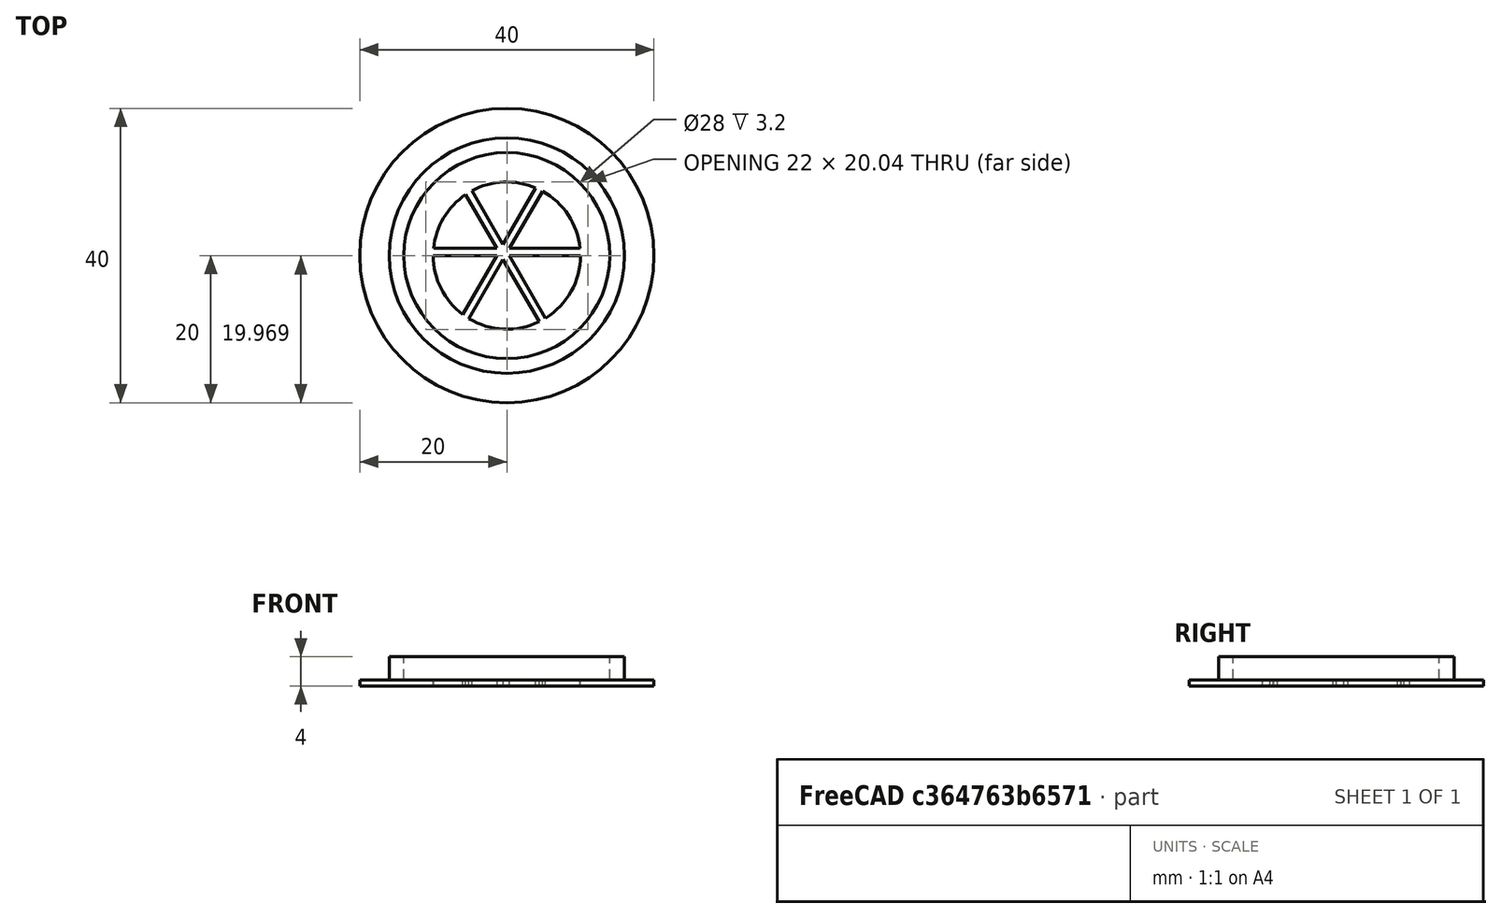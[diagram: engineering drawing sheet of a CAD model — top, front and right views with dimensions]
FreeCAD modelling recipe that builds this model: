
FCSTD DOCUMENT  (FreeCAD 0.17R13541 (Git))
Label: valve bottom 01
License: All rights reserved
LicenseURL: http://en.wikipedia.org/wiki/All_rights_reserved
objects: Part::Cylinder×4, Part::Box×3, Part::Cut×2, Part::MultiFuse×1
note: 10 computed .brp shape members not serialized (recipe doc carries the construction recipe); baked Part::Feature solids carry a one-line shape summary decoded from their .brp

FEATURE [Part::Cylinder] Cylinder  label="plate_flat"
  Angle = 360
  AttacherType = Attacher::AttachEngine3D
  Height = 0.8
  Radius = 20
FEATURE [Part::Cylinder] Cylinder001  label="hole"
  Angle = 360
  AttacherType = Attacher::AttachEngine3D
  Height = 1
  Radius = 10
FEATURE [Part::Cut] Cut  label="plate"
  Base = -> Cylinder
  Tool = -> Cylinder001
FEATURE [Part::Cylinder] Cylinder002  label="shoulder_out"
  Angle = 360
  AttacherType = Attacher::AttachEngine3D
  Height = 4
  Radius = 16
FEATURE [Part::Cylinder] Cylinder003  label="shoulder_in"
  Angle = 360
  AttacherType = Attacher::AttachEngine3D
  Height = 4
  Radius = 14
FEATURE [Part::Cut] Cut001  label="shoulder"
  Base = -> Cylinder002
  Tool = -> Cylinder003
FEATURE [Part::Box] Box  label="cross_1"
  AttacherType = Attacher::AttachEngine3D
  Height = 0.8
  Length = 22
  Placement = pos=(-11,0,0) rot=(0,0,1;0rad)
  Width = 1
FEATURE [Part::Box] Box001  label="cross_002"
  AttacherType = Attacher::AttachEngine3D
  Height = 0.8
  Length = 22
  Placement = pos=(-6,-10,0) rot=(0,0,1;1.0472rad)
  Width = 1
FEATURE [Part::Box] Box002  label="cross_003"
  AttacherType = Attacher::AttachEngine3D
  Height = 0.8
  Length = 22
  Placement = pos=(-6,9,0) rot=(0,0,1;-1.0472rad)
  Width = 1
FEATURE [Part::MultiFuse] Fusion  label="Bottom"
  Shapes = -> [Cut,Box,Box001,Box002,Cut001]
